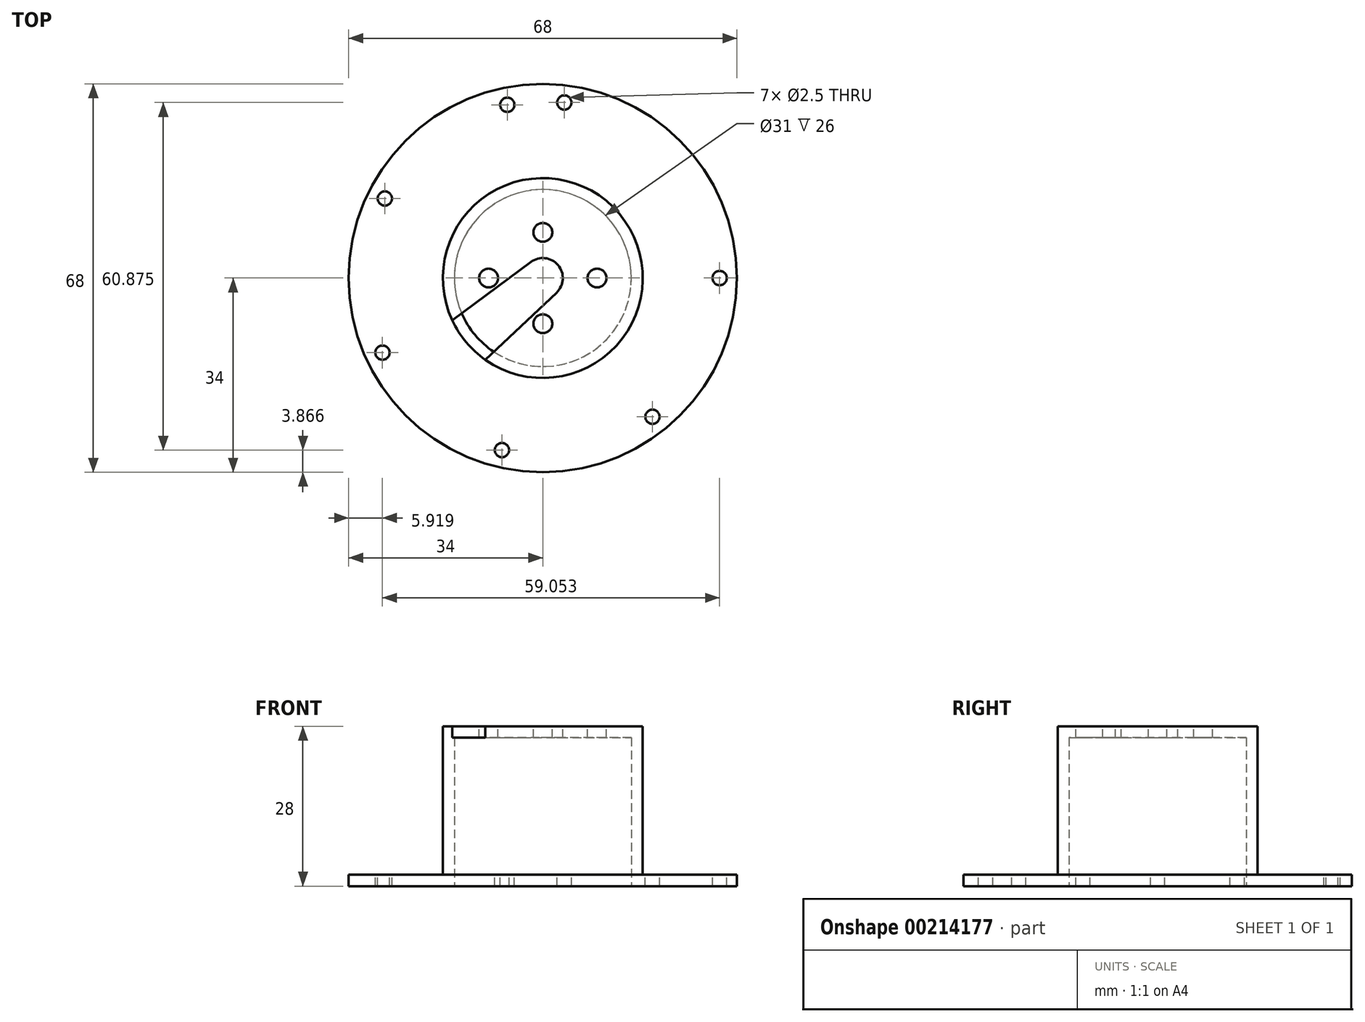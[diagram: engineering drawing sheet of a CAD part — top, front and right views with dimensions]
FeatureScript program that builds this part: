
annotation { "Feature Type Name" : "Feature", "Feature Type Description" : "" }
export const myFeature = defineFeature(function(context is Context, id is Id, definition is map)
    precondition{}
    {
        {
            assignVariable(context, id + "F0", {"name" : "motor_depth", "anyValue" : 24 * mm});
        }
        {
            assignVariable(context, id + "F1", {"name" : "wall_width", "anyValue" : 2 * mm});
        }
        {
            var Q0;
            Q0=qCreatedBy(makeId("Top.planeOp"),FACE);
            var sketch = newSketch(context, id + "F2", { "sketchPlane" : qUnion([Q0])});
            skCircle(sketch, "E0", {"center": v(0, 0) * mm, "radius": 34 * mm});
            skCircle(sketch, "E1", {"center": v(0, 0) * mm, "radius": 17.5 * mm});
            skSolve(sketch);
        }
        {
            var Q0;
            Q0=makeQuery(id+"F2.imprint","IMPRINT",FACE,{"disambiguationData":[TD([[makeQuery(id+"F2.imprint","IMPRINT",EDGE,{"derivedFrom":sQuery(id+"F2.wireOp",EDGE,"E1")}),1.0]])]});
            extrude(context, id + "F3", {"entities" : qUnion([Q0]), "depth" : getVariable(context, 'motor_depth') + getVariable(context, 'wall_width') * 2});
        }
        {
            var Q0;
            Q0=makeQuery(id+"F3.opExtrude","CAP_FACE",FACE,{"disambiguationData":[OSD([sQuery(id+"F2.wireOp",EDGE,"E1")])],"isStart":true});
            shell(context, id + "F4", {"entities" : qUnion([Q0]), "thickness" : getVariable(context, 'wall_width')});
        }
        {
            var Q0;
            Q0=makeQuery(id+"F3.opExtrude","CAP_FACE",FACE,{"disambiguationData":[OSD([sQuery(id+"F2.wireOp",EDGE,"E1")])],"isStart":false});
            var sketch = newSketch(context, id + "F5", { "sketchPlane" : qUnion([Q0])});
            skPoint(sketch, "E2.0", {"position": v(0, 0) * mm});
            skPoint(sketch, "E3", {"position": v(-9.5, 0) * mm});
            skPoint(sketch, "E4", {"position": v(0, 8) * mm});
            skPoint(sketch, "E5.MirrorP", {"position": v(9.5, 0) * mm});
            skPoint(sketch, "E6.MirrorP", {"position": v(0, -8) * mm});
            skLineSegment(sketch, "E7", {"start": v(0, 0) * mm, "end": v(-13.4, -11.25) * mm, "construction": true});
            skLineSegment(sketch, "E8", {"start": v(-2.09, 2.8) * mm, "end": v(-15.85, -7.42) * mm});
            skLineSegment(sketch, "E9.MirrorCS", {"start": v(2.4, -2.54) * mm, "end": v(-10.06, -14.32) * mm});
            skArc(sketch, "E10", {"start": v(-2.09, 2.8) * mm, "mid": v(2.68, 2.25) * mm, "end": v(2.4, -2.54) * mm});
            skLineSegment(sketch, "E11", {"start": v(-15.85, -7.42) * mm, "end": v(-10.06, -14.32) * mm, "construction": true});
            skSolve(sketch);
        }
        {
            var Q0;
            Q0=sQuery(id+"F5.wireOp",VERTEX,"E4");
            var Q1;
            Q1=sQuery(id+"F5.wireOp",VERTEX,"E3");
            var Q2;
            Q2=sQuery(id+"F5.wireOp",VERTEX,"E6.MirrorP");
            var Q3;
            Q3=sQuery(id+"F5.wireOp",VERTEX,"E5.MirrorP");
            var Q4;
            Q4=makeQuery(id+"F3.opExtrude","SWEPT_BODY",BODY,{"disambiguationData":[OSD([sQuery(id+"F2.wireOp",EDGE,"E1")])]});
            hole(context, id + "F6", {"style" : HoleStyle.SIMPLE, "endStyle" : HoleEndStyle.THROUGH, "standardTappedOrClearance" : lookupTablePath({ "standard" : "ISO", "fit" : "Normal", "size" : "M3", "type" : "Clearance" }), "standardBlindInLast" : lookupTablePath({ "fit" : "Standard", "standard" : "ISO", "size" : "M3", "type" : "Clearance" }), "holeDiameter" : 3.3 * mm, "startFromSketch" : true, "locations" : qUnion([Q0, Q1, Q2, Q3]), "scope" : qUnion([Q4]), "isTappedThrough" : true});
        }
        {
            var Q0;
            Q0=makeQuery(id+"F2.imprint","IMPRINT",FACE,{"disambiguationData":[TD([[makeQuery(id+"F2.imprint","IMPRINT",EDGE,{"derivedFrom":sQuery(id+"F2.wireOp",EDGE,"E0")}),1.0]])]});
            extrude(context, id + "F7", {"entities" : qUnion([Q0]), "operationType" : NewBodyOperationType.ADD, "depth" : getVariable(context, 'wall_width')});
        }
        {
            var Q0;
            Q0=makeQuery(id+"F7.opExtrude","CAP_FACE",FACE,{"disambiguationData":[OSD([sQuery(id+"F2.wireOp",EDGE,"E0"),sQuery(id+"F2.wireOp",EDGE,"E1")])],"isStart":false});
            var sketch = newSketch(context, id + "F8", { "sketchPlane" : qUnion([Q0])});
            skPoint(sketch, "E12.center", {"position": v(0, 0) * mm});
            skLineSegment(sketch, "E12.anchor1", {"start": v(0, 0) * mm, "end": v(-7.16, -30.13) * mm, "construction": true});
            skLineSegment(sketch, "E13", {"start": v(0, 0) * mm, "end": v(-28.08, -13.07) * mm, "construction": true});
            skLineSegment(sketch, "E14", {"start": v(0, 0) * mm, "end": v(-27.66, 13.93) * mm, "construction": true});
            skLineSegment(sketch, "E15", {"start": v(-6.22, 30.34) * mm, "end": v(0, 0) * mm, "construction": true});
            skLineSegment(sketch, "E16", {"start": v(0, 0) * mm, "end": v(3.77, 30.74) * mm, "construction": true});
            skLineSegment(sketch, "E17", {"start": v(30.97, 0) * mm, "end": v(0, 0) * mm, "construction": true});
            skLineSegment(sketch, "E18", {"start": v(19.2, -24.3) * mm, "end": v(0, 0) * mm, "construction": true});
            skLineSegment(sketch, "E19", {"start": v(30.97, 0) * mm, "end": v(19.2, -24.3) * mm, "construction": true});
            skLineSegment(sketch, "E20", {"start": v(19.2, -24.3) * mm, "end": v(-7.16, -30.13) * mm, "construction": true});
            skLineSegment(sketch, "E21", {"start": v(-7.16, -30.13) * mm, "end": v(-28.08, -13.07) * mm, "construction": true});
            skLineSegment(sketch, "E22", {"start": v(-28.08, -13.07) * mm, "end": v(-27.66, 13.93) * mm, "construction": true});
            skLineSegment(sketch, "E23", {"start": v(-27.66, 13.93) * mm, "end": v(-6.22, 30.34) * mm, "construction": true});
            skLineSegment(sketch, "E24", {"start": v(30.97, 0) * mm, "end": v(-6.22, 30.34) * mm, "construction": true});
            skLineSegment(sketch, "E25", {"start": v(3.77, 30.74) * mm, "end": v(-6.22, 30.34) * mm, "construction": true});
            skSolve(sketch);
        }
        {
            var Q0;
            Q0=sQuery(id+"F8.wireOp",VERTEX,"E15.start");
            var Q1;
            Q1=sQuery(id+"F8.wireOp",VERTEX,"E22.end");
            var Q2;
            Q2=sQuery(id+"F8.wireOp",VERTEX,"E13.end");
            var Q3;
            Q3=sQuery(id+"F8.wireOp",VERTEX,"E12.anchor1.end");
            var Q4;
            Q4=sQuery(id+"F8.wireOp",VERTEX,"E18.start");
            var Q5;
            Q5=sQuery(id+"F8.wireOp",VERTEX,"E17.start");
            var Q6;
            Q6=sQuery(id+"F8.wireOp",VERTEX,"E16.end");
            var Q7;
            Q7=makeQuery(id+"F3.opExtrude","SWEPT_BODY",BODY,{"disambiguationData":[OSD([sQuery(id+"F2.wireOp",EDGE,"E1")])]});
            hole(context, id + "F9", {"style" : HoleStyle.SIMPLE, "endStyle" : HoleEndStyle.THROUGH, "holeDiameter" : 2.5 * mm, "startFromSketch" : true, "locations" : qUnion([Q0, Q1, Q2, Q3, Q4, Q5, Q6]), "scope" : qUnion([Q7]), "isTappedThrough" : true});
        }
        {
            var Q0;
            {var subQ0=sQuery(id+"F5.wireOp",EDGE,"E8");Q0=makeQuery(id+"F5.imprint","IMPRINT",FACE,{"disambiguationData":[TD([[makeQuery(id+"F5.imprint","IMPRINT",EDGE,{"derivedFrom":subQ0}),1.0]])]});}
            var Q1;
            {var subQ0=sQuery(id+"F2.wireOp",EDGE,"E1");Q1=makeQuery(id+"F4.opShell","OFFSET_FACE",FACE,{"disambiguationData":[OSD([subQ0]),TDD([makeQuery(id+"F3.opExtrude","CAP_FACE",FACE,{"disambiguationData":[OSD([subQ0])],"isStart":false})])]});}
            extrude(context, id + "F10", {"entities" : qUnion([Q0]), "operationType" : NewBodyOperationType.REMOVE, "endBound" : BoundingType.UP_TO_SURFACE, "oppositeDirection" : true, "endBoundEntityFace" : qUnion([Q1]), "depth" : getVariable(context, 'wall_width')});
        }
    });
